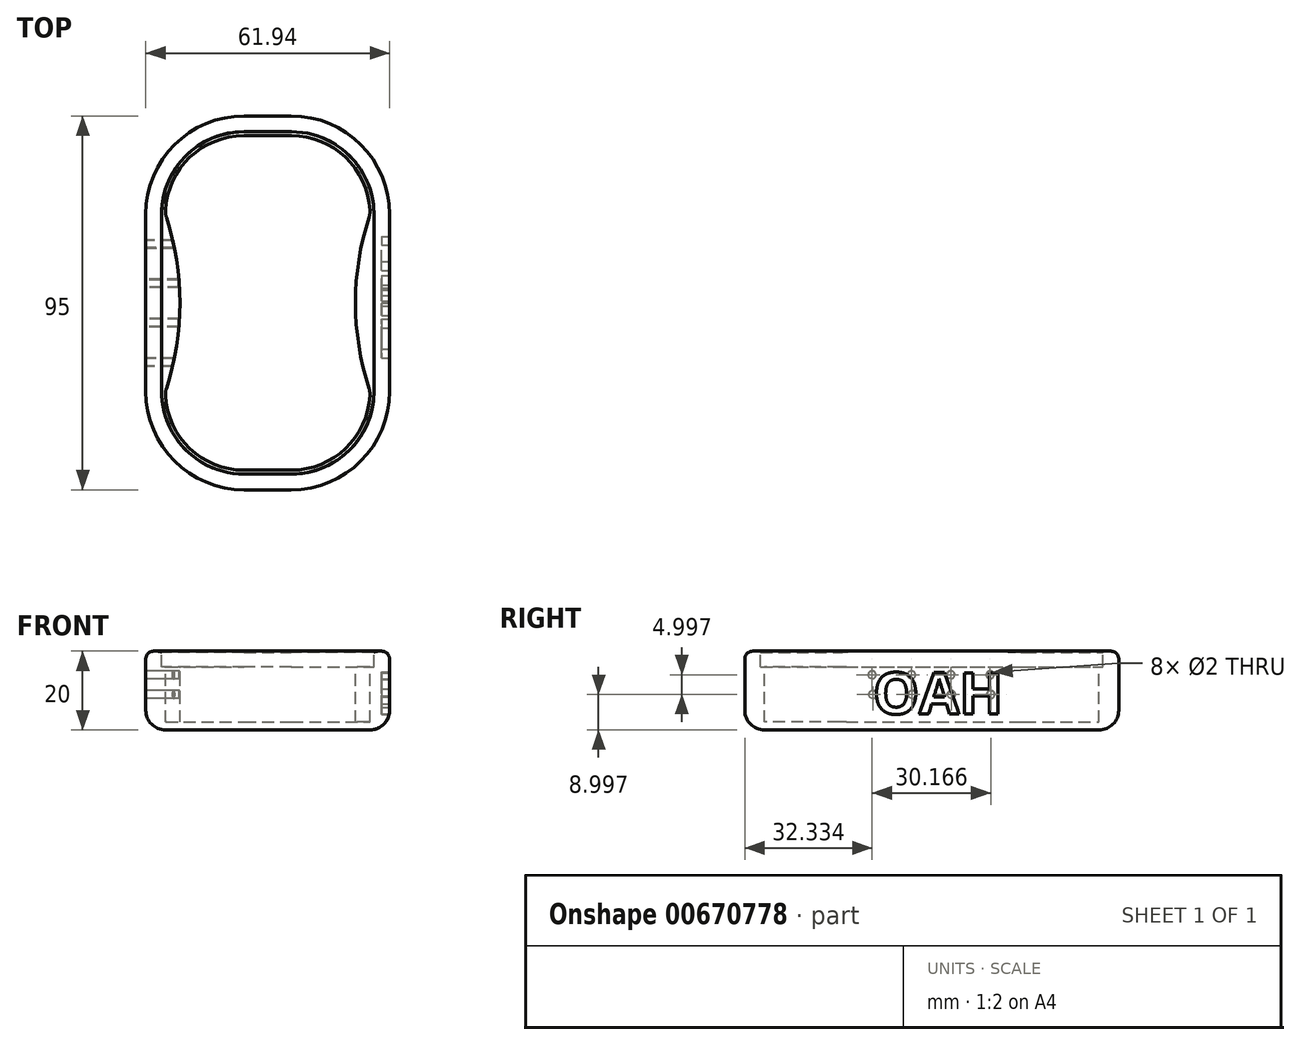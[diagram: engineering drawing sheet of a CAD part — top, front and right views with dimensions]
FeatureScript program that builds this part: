
annotation { "Feature Type Name" : "Feature", "Feature Type Description" : "" }
export const myFeature = defineFeature(function(context is Context, id is Id, definition is map)
    precondition{}
    {
        {
            var Q0;
            Q0=qCreatedBy(makeId("Top.planeOp"),FACE);
            cPlane(context, id + "F0", {"entities" : qUnion([Q0]), "cplaneType" : CPlaneType.OFFSET, "offset" : 20 * mm, "oppositeDirection" : true, "width" : 150 * mm, "height" : 150 * mm});
        }
        {
            var Q0;
            Q0=qCreatedBy(makeId("Top.planeOp"),FACE);
            var sketch = newSketch(context, id + "F1", { "sketchPlane" : qUnion([Q0])});
            skLineSegment(sketch, "E0", {"start": v(0, 100) * mm, "end": v(0, 85) * mm});
            skLineSegment(sketch, "E1", {"start": v(-95.53, 0) * mm, "end": v(0, 0) * mm});
            skLineSegment(sketch, "E2.bottom", {"start": v(20, 0) * mm, "end": v(32, 0) * mm});
            skLineSegment(sketch, "E2.top", {"start": v(20, 85) * mm, "end": v(32, 85) * mm});
            skPoint(sketch, "E3.visualSharp", {"position": v(0, 85) * mm});
            skArc(sketch, "E3.filletArc", {"start": v(20, 85) * mm, "mid": v(6.22, 79.5) * mm, "end": v(0.03, 66) * mm});
            skPoint(sketch, "E4.visualSharp", {"position": v(52, 85) * mm});
            skArc(sketch, "E4.filletArc", {"start": v(51.97, 66) * mm, "mid": v(45.78, 79.5) * mm, "end": v(32, 85) * mm});
            skPoint(sketch, "E5.visualSharp", {"position": v(0, 0) * mm});
            skArc(sketch, "E5.filletArc", {"start": v(0.03, 19) * mm, "mid": v(6.22, 5.5) * mm, "end": v(20, 0) * mm});
            skPoint(sketch, "E6.visualSharp", {"position": v(52, 0) * mm});
            skArc(sketch, "E6.filletArc", {"start": v(32, 0) * mm, "mid": v(45.78, 5.5) * mm, "end": v(51.97, 19) * mm});
            skArc(sketch, "E7", {"start": v(0.27, 20.8) * mm, "mid": v(3.71, 42.5) * mm, "end": v(0.27, 64.2) * mm});
            skArc(sketch, "E8", {"start": v(51.73, 64.2) * mm, "mid": v(48.29, 42.5) * mm, "end": v(51.73, 20.8) * mm});
            skLineSegment(sketch, "E9.trimOffspring", {"start": v(0, 0) * mm, "end": v(0, -100) * mm});
            skLineSegment(sketch, "E10.trimOffspring", {"start": v(52, 0) * mm, "end": v(104.47, 0) * mm});
            skPoint(sketch, "E11.visualSharp", {"position": v(52, 20) * mm});
            skArc(sketch, "E11.filletArc", {"start": v(51.97, 19) * mm, "mid": v(51.94, 19.9) * mm, "end": v(51.73, 20.8) * mm});
            skPoint(sketch, "E12.visualSharp", {"position": v(0, 20) * mm});
            skArc(sketch, "E12.filletArc", {"start": v(0.27, 20.8) * mm, "mid": v(0.06, 19.9) * mm, "end": v(0.03, 19) * mm});
            skPoint(sketch, "E13.visualSharp", {"position": v(0, 65) * mm});
            skArc(sketch, "E13.filletArc", {"start": v(0.03, 66) * mm, "mid": v(0.06, 65.1) * mm, "end": v(0.27, 64.2) * mm});
            skPoint(sketch, "E14.visualSharp", {"position": v(52, 65) * mm});
            skArc(sketch, "E14.filletArc", {"start": v(51.73, 64.2) * mm, "mid": v(51.94, 65.1) * mm, "end": v(51.97, 66) * mm});
            skSolve(sketch);
        }
        {
            var Q0;
            Q0=qCreatedBy(id+"F0.planeOp",FACE);
            var sketch = newSketch(context, id + "F2", { "sketchPlane" : qUnion([Q0])});
            skLineSegment(sketch, "E15.bottom", {"start": v(-4.97, 90) * mm, "end": v(56.97, 90) * mm});
            skLineSegment(sketch, "E15.top", {"start": v(-4.97, -5) * mm, "end": v(56.97, -5) * mm});
            skLineSegment(sketch, "E15.left", {"start": v(-4.97, 90) * mm, "end": v(-4.97, -5) * mm});
            skLineSegment(sketch, "E15.right", {"start": v(56.97, 90) * mm, "end": v(56.97, -5) * mm});
            skSolve(sketch);
        }
        {
            var Q0;
            Q0 = qSketchRegion(id + "F2", true);
            extrude(context, id + "F3", {"entities" : qUnion([Q0]), "depth" : 20 * mm, "offsetDistance" : 25 * mm});
        }
        {
            var Q0;
            Q0=makeQuery(id+"F1.imprint","IMPRINT",FACE,{"disambiguationData":[TD([[makeQuery(id+"F1.imprint","IMPRINT",EDGE,{"derivedFrom":sQuery(id+"F1.wireOp",EDGE,"E2.top")}),-1.0]])]});
            var Q1;
            Q1 = qSketchRegion(id + "F2", true);
            extrude(context, id + "F4", {"entities" : qUnion([Q0, Q1]), "operationType" : NewBodyOperationType.REMOVE, "oppositeDirection" : true, "depth" : 18 * mm, "offsetDistance" : 25 * mm});
        }
        {
            var Q0;
            Q0=makeQuery(id+"F3.opExtrude","SWEPT_EDGE",EDGE,{"disambiguationData":[OSD([sQuery(id+"F2.wireOp",EDGE,"E15.top"),sQuery(id+"F2.wireOp",EDGE,"E15.left")])]});
            var Q1;
            Q1=makeQuery(id+"F3.opExtrude","SWEPT_EDGE",EDGE,{"disambiguationData":[OSD([sQuery(id+"F2.wireOp",EDGE,"E15.bottom"),sQuery(id+"F2.wireOp",EDGE,"E15.right")])]});
            var Q2;
            Q2=makeQuery(id+"F3.opExtrude","SWEPT_EDGE",EDGE,{"disambiguationData":[OSD([sQuery(id+"F2.wireOp",EDGE,"E15.bottom"),sQuery(id+"F2.wireOp",EDGE,"E15.left")])]});
            var Q3;
            Q3=makeQuery(id+"F3.opExtrude","SWEPT_EDGE",EDGE,{"disambiguationData":[OSD([sQuery(id+"F2.wireOp",EDGE,"E15.top"),sQuery(id+"F2.wireOp",EDGE,"E15.right")])]});
            fillet(context, id + "F5", {"entities" : qUnion([Q0, Q1, Q2, Q3]), "radius" : 25 * mm, "tangentPropagation" : true, "allowEdgeOverflow" : false});
        }
        {
            var Q0;
            Q0=makeQuery(id+"F3.opExtrude","SWEPT_FACE",FACE,{"disambiguationData":[OSD([sQuery(id+"F2.wireOp",EDGE,"E15.right")])]});
            var sketch = newSketch(context, id + "F6", { "sketchPlane" : qUnion([Q0])});
            skText(sketch, "E16", { "text": "OAH", "fontName": "OpenSans-Bold.ttf"});
            const initialGuessF6  = {"E16": [0.0276, -0.01596, 1, 0, 0.01058]};
            skSetInitialGuess(sketch, initialGuessF6);
            skSolve(sketch);
        }
        {
            var Q0;
            Q0 = qSketchRegion(id + "F6", true);
            extrude(context, id + "F7", {"entities" : qUnion([Q0]), "operationType" : NewBodyOperationType.REMOVE, "oppositeDirection" : true, "depth" : 2 * mm, "offsetDistance" : 25 * mm});
        }
        {
            var Q0;
            {var subQ0=sQuery(id+"F2.wireOp",EDGE,"E15.right");var subQ1=sQuery(id+"F2.wireOp",EDGE,"E15.top");Q0=makeQuery(id+"F5.opFillet","BLEND_EDGE",EDGE,{"blendedFrom":[makeQuery(id+"F3.opExtrude","SWEPT_EDGE",EDGE,{"disambiguationData":[OSD([subQ1,subQ0])]}),makeQuery(id+"F3.opExtrude","CAP_FACE",FACE,{"disambiguationData":[OSD([sQuery(id+"F2.wireOp",EDGE,"E15.bottom"),subQ1,sQuery(id+"F2.wireOp",EDGE,"E15.left"),subQ0])],"isStart":true})],"blendedInto":[makeQuery(id+"F3.opExtrude","CAP_FACE",FACE,{"disambiguationData":[OSD([sQuery(id+"F2.wireOp",EDGE,"E15.bottom"),subQ1,sQuery(id+"F2.wireOp",EDGE,"E15.left"),subQ0])],"isStart":true})]});}
            fillet(context, id + "F8", {"entities" : qUnion([Q0]), "radius" : 5 * mm, "tangentPropagation" : true, "allowEdgeOverflow" : false});
        }
        {
            var Q0;
            Q0=makeQuery(id+"F3.opExtrude","CAP_FACE",FACE,{"disambiguationData":[OSD([sQuery(id+"F2.wireOp",EDGE,"E15.bottom"),sQuery(id+"F2.wireOp",EDGE,"E15.top"),sQuery(id+"F2.wireOp",EDGE,"E15.left"),sQuery(id+"F2.wireOp",EDGE,"E15.right")])],"isStart":false});
            var Q1;
            {var subQ0=sQuery(id+"F2.wireOp",EDGE,"E15.left");var subQ1=sQuery(id+"F2.wireOp",EDGE,"E15.top");Q1=makeQuery(id+"F5.opFillet","BLEND_EDGE",EDGE,{"blendedFrom":[makeQuery(id+"F3.opExtrude","SWEPT_EDGE",EDGE,{"disambiguationData":[OSD([subQ1,subQ0])]}),makeQuery(id+"F3.opExtrude","CAP_FACE",FACE,{"disambiguationData":[OSD([sQuery(id+"F2.wireOp",EDGE,"E15.bottom"),subQ1,subQ0,sQuery(id+"F2.wireOp",EDGE,"E15.right")])],"isStart":false})],"blendedInto":[makeQuery(id+"F3.opExtrude","CAP_FACE",FACE,{"disambiguationData":[OSD([sQuery(id+"F2.wireOp",EDGE,"E15.bottom"),subQ1,subQ0,sQuery(id+"F2.wireOp",EDGE,"E15.right")])],"isStart":false})]});}
            fillet(context, id + "F9", {"entities" : qUnion([Q0, Q1]), "radius" : 2 * mm, "tangentPropagation" : true, "allowEdgeOverflow" : false});
        }
        {
            var Q0;
            Q0=makeQuery(id+"F3.opExtrude","SWEPT_FACE",FACE,{"disambiguationData":[OSD([sQuery(id+"F2.wireOp",EDGE,"E15.left")])]});
            var sketch = newSketch(context, id + "F10", { "sketchPlane" : qUnion([Q0])});
            skCircle(sketch, "E17", {"center": v(-57.67, -16) * mm, "radius": 1 * mm});
            skCircle(sketch, "E18.0.1.0", {"center": v(-57.5, -11) * mm, "radius": 1 * mm});
            skCircle(sketch, "E18.0.2.0", {"center": v(-57.33, -6) * mm, "radius": 1 * mm});
            skCircle(sketch, "E18.1.0.0", {"center": v(-47.67, -16) * mm, "radius": 1 * mm});
            skCircle(sketch, "E18.1.1.0", {"center": v(-47.5, -11) * mm, "radius": 1 * mm});
            skCircle(sketch, "E18.1.2.0", {"center": v(-47.33, -6) * mm, "radius": 1 * mm});
            skCircle(sketch, "E18.2.0.0", {"center": v(-37.67, -16) * mm, "radius": 1 * mm});
            skCircle(sketch, "E18.2.1.0", {"center": v(-37.5, -11) * mm, "radius": 1 * mm});
            skCircle(sketch, "E18.2.2.0", {"center": v(-37.33, -6) * mm, "radius": 1 * mm});
            skLineSegment(sketch, "E18.direction1", {"start": v(-57.67, -16) * mm, "end": v(-47.67, -16) * mm, "construction": true});
            skLineSegment(sketch, "E18.direction2", {"start": v(-57.67, -16) * mm, "end": v(-57.5, -11) * mm, "construction": true});
            skCircle(sketch, "E19.0.3.0", {"center": v(-27.67, -16) * mm, "radius": 1 * mm});
            skCircle(sketch, "E19.0.3.1", {"center": v(-27.5, -11) * mm, "radius": 1 * mm});
            skCircle(sketch, "E19.0.3.2", {"center": v(-27.33, -6) * mm, "radius": 1 * mm});
            skSolve(sketch);
        }
        {
            var Q0;
            Q0=makeQuery(id+"F10.imprint","IMPRINT",FACE,{"disambiguationData":[TD([[makeQuery(id+"F10.imprint","IMPRINT",EDGE,{"derivedFrom":sQuery(id+"F10.wireOp",EDGE,"E18.0.1.0")}),1.0]])]});
            var Q1;
            Q1=makeQuery(id+"F10.imprint","IMPRINT",FACE,{"disambiguationData":[TD([[makeQuery(id+"F10.imprint","IMPRINT",EDGE,{"derivedFrom":sQuery(id+"F10.wireOp",EDGE,"E18.1.1.0")}),1.0]])]});
            var Q2;
            Q2=makeQuery(id+"F10.imprint","IMPRINT",FACE,{"disambiguationData":[TD([[makeQuery(id+"F10.imprint","IMPRINT",EDGE,{"derivedFrom":sQuery(id+"F10.wireOp",EDGE,"E18.1.2.0")}),1.0]])]});
            var Q3;
            Q3=makeQuery(id+"F10.imprint","IMPRINT",FACE,{"disambiguationData":[TD([[makeQuery(id+"F10.imprint","IMPRINT",EDGE,{"derivedFrom":sQuery(id+"F10.wireOp",EDGE,"E18.2.1.0")}),1.0]])]});
            var Q4;
            Q4=makeQuery(id+"F10.imprint","IMPRINT",FACE,{"disambiguationData":[TD([[makeQuery(id+"F10.imprint","IMPRINT",EDGE,{"derivedFrom":sQuery(id+"F10.wireOp",EDGE,"E18.2.2.0")}),1.0]])]});
            var Q5;
            Q5=makeQuery(id+"F10.imprint","IMPRINT",FACE,{"disambiguationData":[TD([[makeQuery(id+"F10.imprint","IMPRINT",EDGE,{"derivedFrom":sQuery(id+"F10.wireOp",EDGE,"E19.0.3.1")}),1.0]])]});
            var Q6;
            Q6=makeQuery(id+"F10.imprint","IMPRINT",FACE,{"disambiguationData":[TD([[makeQuery(id+"F10.imprint","IMPRINT",EDGE,{"derivedFrom":sQuery(id+"F10.wireOp",EDGE,"E19.0.3.2")}),1.0]])]});
            var Q7;
            Q7=makeQuery(id+"F10.imprint","IMPRINT",FACE,{"disambiguationData":[TD([[makeQuery(id+"F10.imprint","IMPRINT",EDGE,{"derivedFrom":sQuery(id+"F10.wireOp",EDGE,"E18.0.2.0")}),1.0]])]});
            var Q8;
            Q8=makeQuery(id+"F10.imprint","IMPRINT",FACE,{"disambiguationData":[TD([[makeQuery(id+"F10.imprint","IMPRINT",EDGE,{"derivedFrom":sQuery(id+"F10.wireOp",EDGE,"E17")}),1.0]])]});
            var Q9;
            Q9=makeQuery(id+"F10.imprint","IMPRINT",FACE,{"disambiguationData":[TD([[makeQuery(id+"F10.imprint","IMPRINT",EDGE,{"derivedFrom":sQuery(id+"F10.wireOp",EDGE,"E18.1.0.0")}),1.0]])]});
            var Q10;
            Q10=makeQuery(id+"F10.imprint","IMPRINT",FACE,{"disambiguationData":[TD([[makeQuery(id+"F10.imprint","IMPRINT",EDGE,{"derivedFrom":sQuery(id+"F10.wireOp",EDGE,"E19.0.3.0")}),1.0]])]});
            var Q11;
            Q11=makeQuery(id+"F10.imprint","IMPRINT",FACE,{"disambiguationData":[TD([[makeQuery(id+"F10.imprint","IMPRINT",EDGE,{"derivedFrom":sQuery(id+"F10.wireOp",EDGE,"E18.2.0.0")}),1.0]])]});
            extrude(context, id + "F11", {"entities" : qUnion([Q0, Q1, Q2, Q3, Q4, Q5, Q6, Q7, Q8, Q9, Q10, Q11]), "operationType" : NewBodyOperationType.REMOVE, "endBound" : BoundingType.UP_TO_NEXT, "oppositeDirection" : true, "depth" : 25 * mm, "offsetDistance" : 25 * mm});
        }
        {
            var Q0;
            Q0=qCreatedBy(makeId("Top.planeOp"),FACE);
            var sketch = newSketch(context, id + "F12", { "sketchPlane" : qUnion([Q0])});
            skLineSegment(sketch, "E20.0", {"start": v(52.97, 20) * mm, "end": v(52.97, 65) * mm});
            skArc(sketch, "E20.1", {"start": v(31.97, -1) * mm, "mid": v(46.82, 5.15) * mm, "end": v(52.97, 20) * mm});
            skArc(sketch, "E20.2", {"start": v(52.97, 65) * mm, "mid": v(46.82, 79.85) * mm, "end": v(31.97, 86) * mm});
            skLineSegment(sketch, "E20.3", {"start": v(20.03, -1) * mm, "end": v(31.97, -1) * mm});
            skLineSegment(sketch, "E20.4", {"start": v(31.97, 86) * mm, "end": v(20.03, 86) * mm});
            skArc(sketch, "E20.5", {"start": v(20.03, 86) * mm, "mid": v(5.18, 79.85) * mm, "end": v(-0.97, 65) * mm});
            skLineSegment(sketch, "E20.6", {"start": v(-0.97, 65) * mm, "end": v(-0.97, 20) * mm});
            skArc(sketch, "E20.7", {"start": v(-0.97, 20) * mm, "mid": v(5.18, 5.15) * mm, "end": v(20.03, -1) * mm});
            skSolve(sketch);
        }
        {
            var Q0;
            Q0=makeQuery(id+"F12.imprint","IMPRINT",FACE,{"disambiguationData":[TD([[makeQuery(id+"F12.imprint","IMPRINT",EDGE,{"derivedFrom":sQuery(id+"F12.wireOp",EDGE,"E20.0")}),1.0]])]});
            extrude(context, id + "F13", {"entities" : qUnion([Q0]), "operationType" : NewBodyOperationType.REMOVE, "oppositeDirection" : true, "depth" : 4 * mm, "offsetDistance" : 25 * mm});
        }
    });
